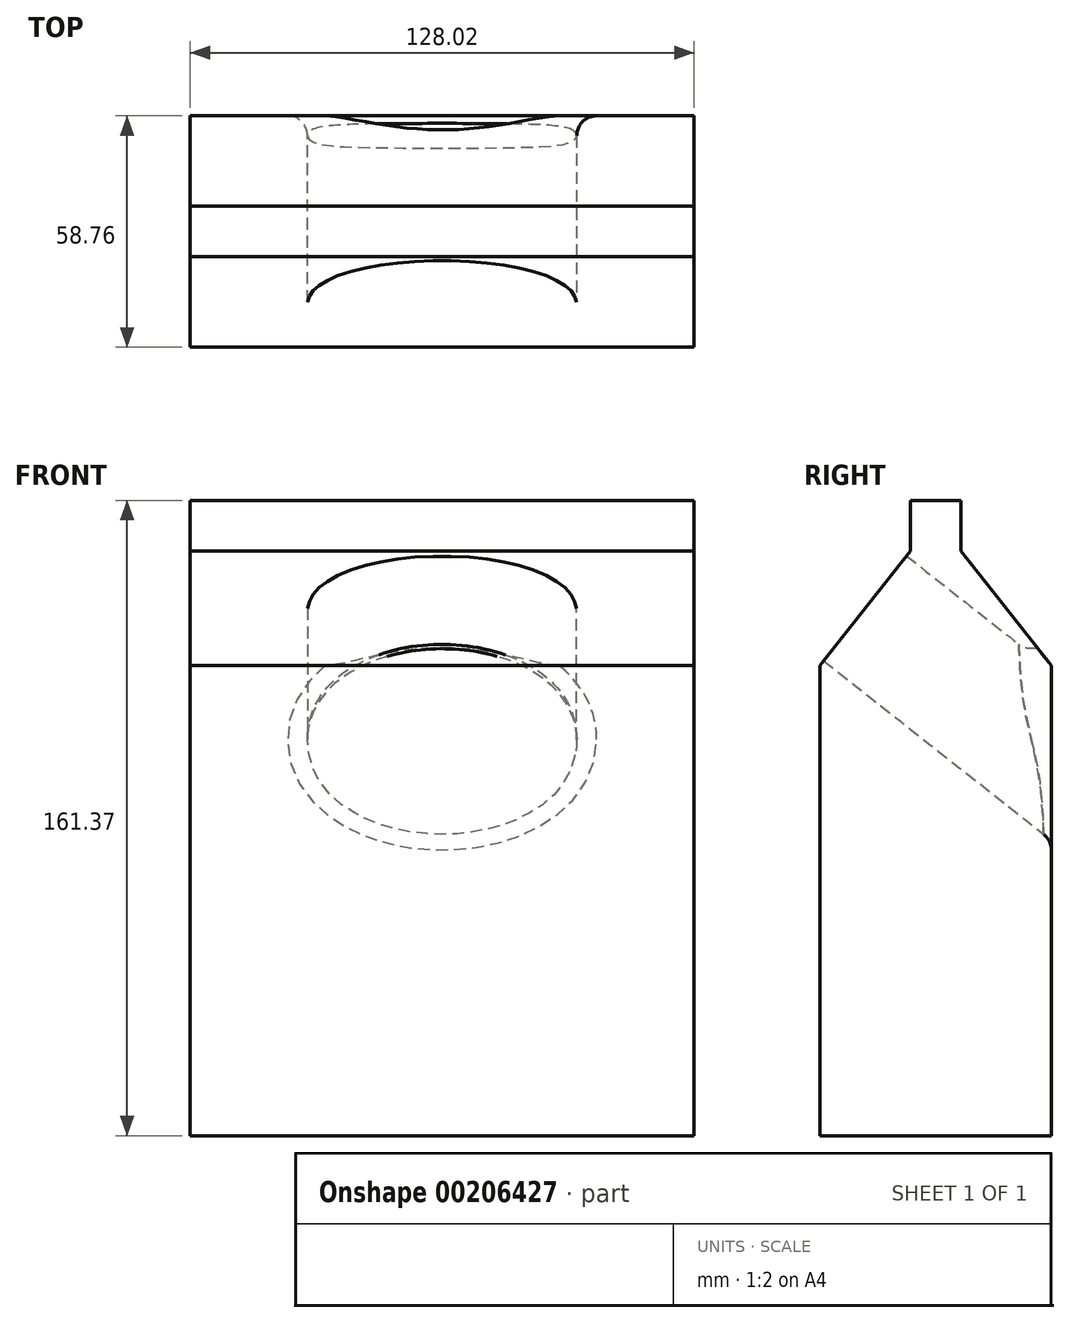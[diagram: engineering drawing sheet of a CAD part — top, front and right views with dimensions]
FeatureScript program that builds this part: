
annotation { "Feature Type Name" : "Feature", "Feature Type Description" : "" }
export const myFeature = defineFeature(function(context is Context, id is Id, definition is map)
    precondition{}
    {
        {
            var Q0;
            Q0=qCreatedBy(makeId("Right.planeOp"),FACE);
            var sketch = newSketch(context, id + "F0", { "sketchPlane" : qUnion([Q0])});
            skLineSegment(sketch, "E0.top", {"start": v(29.38, -96.43) * mm, "end": v(-29.38, -96.43) * mm});
            skLineSegment(sketch, "E0.left", {"start": v(29.38, 22.97) * mm, "end": v(29.38, -96.43) * mm});
            skLineSegment(sketch, "E0.right", {"start": v(-29.38, 22.97) * mm, "end": v(-29.38, -96.43) * mm});
            skPoint(sketch, "E0.middle", {"position": v(0, -36.73) * mm});
            skLineSegment(sketch, "E1", {"start": v(29.38, 22.97) * mm, "end": v(6.42, 52.1) * mm});
            skLineSegment(sketch, "E2", {"start": v(6.42, 52.1) * mm, "end": v(6.42, 64.94) * mm});
            skLineSegment(sketch, "E3", {"start": v(6.42, 64.94) * mm, "end": v(0, 64.94) * mm});
            skLineSegment(sketch, "E4.MirrorCS", {"start": v(-6.42, 64.94) * mm, "end": v(0, 64.94) * mm});
            skLineSegment(sketch, "E5.MirrorCS", {"start": v(-6.42, 52.1) * mm, "end": v(-6.42, 64.94) * mm});
            skLineSegment(sketch, "E6.MirrorCS", {"start": v(-29.38, 22.97) * mm, "end": v(-6.42, 52.1) * mm});
            skSolve(sketch);
        }
        {
            var Q0;
            Q0=makeQuery(id+"F0.imprint","IMPRINT",FACE,{"disambiguationData":[TD([[makeQuery(id+"F0.imprint","IMPRINT",EDGE,{"derivedFrom":sQuery(id+"F0.wireOp",EDGE,"E0.top")}),-1.0]])]});
            extrude(context, id + "F1", {"entities" : qUnion([Q0]), "endBound" : BoundingType.SYMMETRIC, "depth" : 128.02 * mm});
        }
        {
            var Q0;
            Q0=makeQuery(id+"F1.opExtrude","SWEPT_FACE",FACE,{"disambiguationData":[OSD([sQuery(id+"F0.wireOp",EDGE,"E6.MirrorCS")])]});
            var sketch = newSketch(context, id + "F2", { "sketchPlane" : qUnion([Q0])});
            skEllipse(sketch, "E7", {"center": v(0, 18.4) * mm, "majorRadius": 34.2 * mm, "minorRadius": 16.99 * mm, "majorAxis": v(1, 0)});
            skPoint(sketch, "E8.orphan", {"position": v(-64, 36.94) * mm});
            skPoint(sketch, "E9.end.orphan", {"position": v(64, -0.15) * mm});
            skSolve(sketch);
        }
        {
            var Q0;
            Q0=makeQuery(id+"F2.imprint","IMPRINT",FACE,{"disambiguationData":[TD([[makeQuery(id+"F2.imprint","IMPRINT",EDGE,{"derivedFrom":sQuery(id+"F2.wireOp",EDGE,"E7")}),1.0]])]});
            extrude(context, id + "F3", {"entities" : qUnion([Q0]), "operationType" : NewBodyOperationType.REMOVE, "oppositeDirection" : true, "depth" : 247.4 * mm});
        }
        {
            var Q0;
            Q0=makeQuery(id+"F3.boolean.opBoolean","INTERSECT",EDGE,{"derivedFrom":[makeQuery(id+"F1.opExtrude","SWEPT_FACE",FACE,{"disambiguationData":[OSD([sQuery(id+"F0.wireOp",EDGE,"E0.left")])]}),makeQuery(id+"F3.opExtrude","SWEPT_FACE",FACE,{"disambiguationData":[OSD([sQuery(id+"F2.wireOp",EDGE,"E7")])]})]});
            fillet(context, id + "F4", {"entities" : qUnion([Q0]), "radius" : 5.08 * mm, "tangentPropagation" : true, "allowEdgeOverflow" : false});
        }
    });
